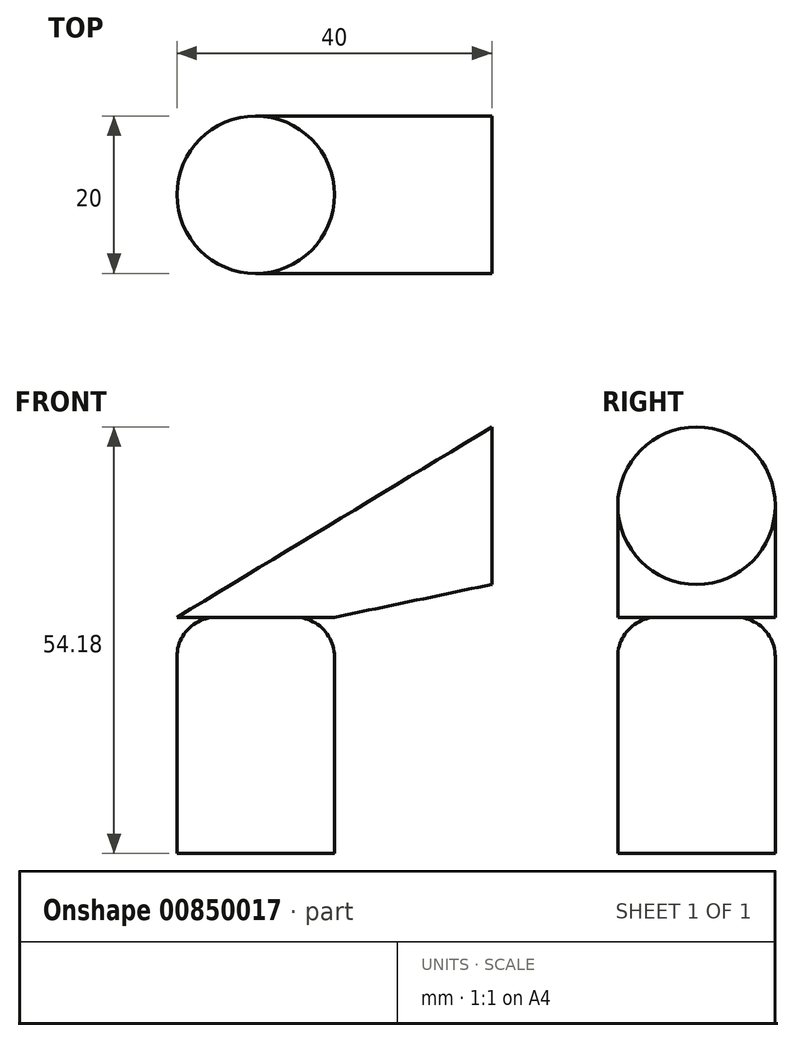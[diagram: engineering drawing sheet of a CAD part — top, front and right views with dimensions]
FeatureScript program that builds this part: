
annotation { "Feature Type Name" : "Feature", "Feature Type Description" : "" }
export const myFeature = defineFeature(function(context is Context, id is Id, definition is map)
    precondition{}
    {
        {
            var Q0;
            Q0=qCreatedBy(makeId("Top.planeOp"),FACE);
            var sketch = newSketch(context, id + "F0", { "sketchPlane" : qUnion([Q0])});
            skCircle(sketch, "E0", {"center": v(0, 0) * mm, "radius": 10 * mm});
            skSolve(sketch);
        }
        {
            var Q0;
            Q0=makeQuery(id+"F0.imprint","IMPRINT",FACE,{"disambiguationData":[TD([[makeQuery(id+"F0.imprint","IMPRINT",EDGE,{"derivedFrom":sQuery(id+"F0.wireOp",EDGE,"E0")}),1.0]])]});
            extrude(context, id + "F1", {"entities" : qUnion([Q0]), "depth" : 30 * mm, "offsetDistance" : 25 * mm});
        }
        {
            var Q0;
            Q0=qCreatedBy(makeId("Right.planeOp"),FACE);
            cPlane(context, id + "F2", {"entities" : qUnion([Q0]), "cplaneType" : CPlaneType.OFFSET, "offset" : 30 * mm, "width" : 150 * mm, "height" : 150 * mm});
        }
        {
            var Q0;
            Q0=qCreatedBy(id+"F2.planeOp",FACE);
            var sketch = newSketch(context, id + "F3", { "sketchPlane" : qUnion([Q0])});
            skCircle(sketch, "E1", {"center": v(0, 44.18) * mm, "radius": 10 * mm});
            skSolve(sketch);
        }
        {
            var Q0;
            Q0=makeQuery(id+"F3.imprint","IMPRINT",FACE,{"disambiguationData":[TD([[makeQuery(id+"F3.imprint","IMPRINT",EDGE,{"derivedFrom":sQuery(id+"F3.wireOp",EDGE,"E1")}),1.0]])]});
            var Q1;
            Q1=makeQuery(id+"F1.opExtrude","CAP_FACE",FACE,{"disambiguationData":[OSD([sQuery(id+"F0.wireOp",EDGE,"E0")])],"isStart":false});
            loft(context, id + "F4", {"sheetProfilesArray" : [{ "sheetProfileEntities" : qUnion([Q0]) }, { "sheetProfileEntities" : qUnion([Q1]) }]});
        }
        {
            var Q0;
            Q0=makeQuery(id+"F1.opExtrude","CAP_EDGE",EDGE,{"disambiguationData":[OSD([sQuery(id+"F0.wireOp",EDGE,"E0")])],"isStart":false});
            fillet(context, id + "F5", {"entities" : qUnion([Q0]), "radius" : 5 * mm, "tangentPropagation" : true, "allowEdgeOverflow" : false});
        }
    });
